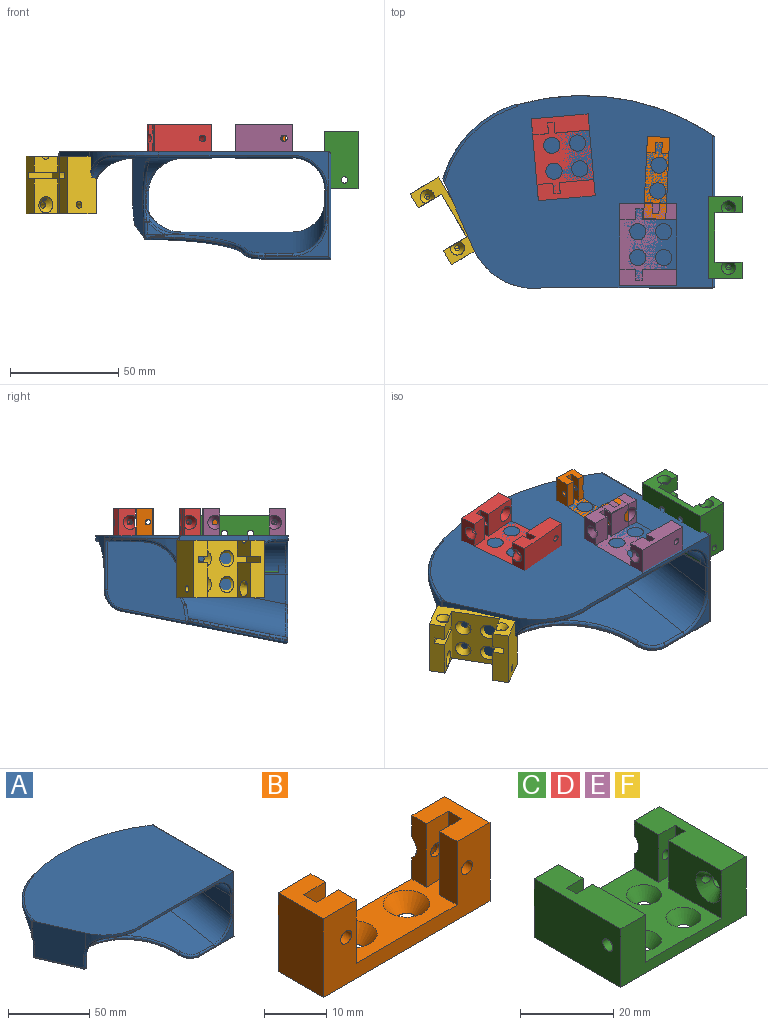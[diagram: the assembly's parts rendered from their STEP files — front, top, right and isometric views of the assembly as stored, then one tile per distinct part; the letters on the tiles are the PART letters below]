
ASSEMBLY  parts=6 mates=3
PART A: 100 faces, bbox 136.9x100.9x51.2 mm
  f0: cylinder r=5mm len=5.41mm, axis (0,-0.19,0.98), area 20.6mm2, adj f1,f2,f13,f83
  f1: bspline ~5.42x5.15mm, area 12.3mm2, adj f0,f2,f13,f60,f78,f84
  f2: plane 10.08x3.37mm, normal (0,0.98,0.19), area 10.7mm2, adj f0,f1,f60,f63
  f3: plane 97.85x87.06mm, normal (0,0,-1), area 6114.5mm2, adj f4,f8,f27,f28,f29,f31,f33,f40
  f4: plane 45.57x36.71mm, normal (-0.99,-0.14,0), area 1163.6mm2, adj f3,f40,f42,f44,f59,f64
  f5: plane 78.53x48.54mm, normal (0,-1,0), area 269.8mm2, adj f12,f19,f34,f38,f39,f46,f47,f48
  f6: cylinder r=107.81mm len=90.77mm, axis (0,0,1), area 314.9mm2, adj f11,f12,f35,f36,f37,f40,f72,f73
  f7: plane 89.44x75.48mm, normal (0,0.19,-0.98), area 2637.8mm2, adj f11,f35,f36,f39,f41,f43,f44,f45
  f8: cylinder r=18.91mm len=29.5mm, axis (0.99,0.14,0), area 177.2mm2, adj f3,f30,f53,f54,f59,f61,f65,f66
  f9: plane 33.93x19.2mm, normal (0.99,0.14,0), area 524.9mm2, adj f14,f15,f33,f53,f61,f70,f71,f72
  f10: plane 59.19x50.35mm, normal (0,-0.19,0.98), area 1600.6mm2, adj f17,f30,f32,f50,f51,f52,f62,f66
  f11: plane 68.7x48.54mm, normal (1,0,0), area 2856.3mm2, adj f6,f7,f35,f37,f38,f39
  f12: plane 123.97x89.25mm, normal (0,0,1), area 9499.2mm2, adj f5,f6,f19,f22,f37,f40,f79
  f13: plane 68.41x19.74mm, normal (-1,0,0), area 730.4mm2, adj f0,f1,f31,f32,f48,f76,f77,f78
  f14: plane 15.18x7.72mm, normal (0,0.98,0.19), area 37.5mm2, adj f9,f15,f60,f61
  f15: plane 28.9x7.23mm, normal (0.99,0.13,0.03), area 44.9mm2, adj f9,f14,f69,f70
  f16: plane 8.4x5.5mm, normal (0,-0.99,0.16), area 20.4mm2, adj f17,f64,f66,f68
  f17: plane 13.1x1.75mm, normal (0,-0.98,-0.19), area 8.4mm2, adj f10,f16,f18,f45,f52,f64
  f18: cylinder r=43.69mm len=43.35mm, axis (0,0.19,-0.98), area 25.3mm2, adj f17,f34,f43,f52
  f19: cylinder r=30.78mm len=32.11mm, axis (0,0,1), area 107.4mm2, adj f5,f12,f22,f85,f86
  f20: plane 2.8x1.15mm, normal (0.99,0.14,0), area 2.6mm2, adj f21,f40,f79,f80
  f21: cylinder r=50.54mm len=34.12mm, axis (0,0,1), area 73.5mm2, adj f20,f79,f80,f81,f82
  f22: plane 31.86x26.8mm, normal (-0.92,-0.4,0), area 902.5mm2, adj f12,f19,f79,f81,f87,f88,f90,f92
  f23: plane 9x0.4mm, normal (-0.2,0.98,0), area 3.7mm2, adj f29,f58,f92,f98
  f24: plane 9x0.37mm, normal (0.4,-0.92,0), area 3.6mm2, adj f27,f55,f56,f88
  f25: plane 29.72x12.99mm, normal (0.92,0.4,0), area 291.9mm2, adj f28,f56,f96,f98
  f26: plane 29.88x13.39mm, normal (0,0,-1), area 13mm2, adj f55,f58,f90,f96
  f27: cylinder r=15mm len=21.22mm, axis (-0.92,-0.4,0), area 128.8mm2, adj f3,f24,f57,f86,f87
  f28: cylinder r=15mm len=62.59mm, axis (0.4,-0.92,0), area 1109.6mm2, adj f3,f25,f57,f99
  f29: cylinder r=15mm len=17.45mm, axis (0.98,0.2,0), area 43.3mm2, adj f3,f23,f82,f93,f99
  f30: bspline ~16.69x14.84mm, area 55mm2, adj f8,f10,f61,f66
  f31: cylinder r=15mm len=77.33mm, axis (0,1,0), area 1716.1mm2, adj f3,f13,f47,f75
  f32: cylinder r=15mm len=52.95mm, axis (0,-0.98,-0.19), area 1164.9mm2, adj f10,f13,f49,f63
  f33: cylinder r=15mm len=55.41mm, axis (0.14,-0.99,0), area 1025.4mm2, adj f3,f9,f54,f73
  f34: bspline ~9.97x8.84mm, area 5.9mm2, adj f5,f18,f41,f51
  f35: bspline ~12.79x11.18mm, area 20.8mm2, adj f6,f7,f11,f77
  f36: bspline ~9.91x8.22mm, area 5.3mm2, adj f6,f7,f42,f70,f71
  f37: cylinder r=1.2mm len=70.71mm, axis (0,-1,0), area 131.4mm2, adj f6,f11,f12,f38
  f38: cylinder r=1.2mm len=49.74mm, axis (0,0,-1), area 91.5mm2, adj f5,f11,f37,f39
  f39: cylinder r=1.2mm len=30.26mm, axis (1,0,0), area 63.2mm2, adj f5,f7,f11,f38,f41
  f40: cylinder r=1.2mm len=25.08mm, axis (0,0,1), area 42.3mm2, adj f3,f4,f6,f12,f20,f42,f79,f80
  f41: bspline ~12.29x9.66mm, area 28.4mm2, adj f7,f34,f39,f43
  f42: bspline ~12.38x10.54mm, area 24mm2, adj f4,f36,f40,f44
  f43: torus R=44.89mm, axis (0,0.19,-0.98), area 120.3mm2, adj f7,f18,f41,f45
  f44: cylinder r=1.2mm len=30.37mm, axis (0.14,-0.97,-0.19), area 58.2mm2, adj f4,f7,f42,f45,f64
  f45: cylinder r=1.2mm len=2.78mm, axis (-1,0,0), area 4.5mm2, adj f7,f17,f43,f44,f64
  f46: cylinder r=1.2mm len=62mm, axis (-1,0,0), area 116.8mm2, adj f3,f5,f47,f85
  f47: torus R=16.2mm, axis (0,-1,0), area 45.7mm2, adj f5,f31,f46,f48
  f48: cylinder r=1.2mm len=13.83mm, axis (0,0,1), area 26.1mm2, adj f5,f13,f47,f49
  f49: bspline ~19.38x16.2mm, area 42.7mm2, adj f5,f32,f48,f50
  f50: cylinder r=1.2mm len=12.47mm, axis (-1,0,0), area 20.6mm2, adj f5,f10,f49,f51
  f51: bspline ~12.28x11.04mm, area 24.3mm2, adj f10,f34,f50,f52
  f52: torus R=44.89mm, axis (0,0.19,-0.98), area 110.5mm2, adj f10,f17,f18,f51
  f53: torus R=20.11mm, axis (-0.99,-0.14,0), area 18.8mm2, adj f8,f9,f54,f61
  f54: bspline ~18.62x18mm, area 21.2mm2, adj f8,f33,f53
  f55: cylinder r=1.2mm len=1.26mm, axis (-0.92,-0.4,0), area 0.8mm2, adj f24,f26,f89,f95
  f56: cylinder r=1.2mm len=9mm, axis (0,0,1), area 17mm2, adj f24,f25,f57,f95
  f57: bspline ~20.85x15.49mm, area 31.4mm2, adj f27,f28,f56
  f58: cylinder r=1.2mm len=1.26mm, axis (0.98,0.2,0), area 0.8mm2, adj f23,f26,f91,f97
  f59: torus R=20.11mm, axis (-0.99,-0.14,0), area 70.2mm2, adj f3,f4,f8,f65
  f60: cylinder r=1.2mm len=83.94mm, axis (1,0,0), area 150.2mm2, adj f1,f2,f7,f14,f62,f69,f84
  f61: bspline ~19.68x13.65mm, area 52.9mm2, adj f8,f9,f14,f30,f53,f62
  f62: cylinder r=1.6mm len=51.53mm, axis (1,0,0), area 129.5mm2, adj f10,f60,f61,f63
  f63: torus R=16.6mm, axis (0,-0.98,-0.19), area 40.2mm2, adj f2,f32,f62,f83
  f64: cylinder r=1.6mm len=8.64mm, axis (0.02,-0.16,-0.99), area 16mm2, adj f4,f16,f17,f44,f45,f65,f67
  f65: bspline ~1.77x1.68mm, area 1.6mm2, adj f8,f59,f64,f67
  f66: bspline ~16.3x8.25mm, area 18.5mm2, adj f8,f10,f16,f30,f68
  f67: bspline ~0.76x0.76mm, area 0.2mm2, adj f64,f65,f68
  f68: bspline ~1.5x0.98mm, area 0.8mm2, adj f8,f16,f66,f67
  f69: cylinder r=1.2mm len=25.05mm, axis (0.14,-0.97,-0.19), area 47.3mm2, adj f7,f15,f60,f70
  f70: bspline ~8.64x4.79mm, area 11.5mm2, adj f9,f15,f36,f69,f71
  f71: bspline ~9.28x4.66mm, area 14.9mm2, adj f9,f36,f70,f72
  f72: cylinder r=1.2mm len=7.26mm, axis (0,0,1), area 14.9mm2, adj f6,f9,f71,f73
  f73: bspline ~18.01x17.92mm, area 47.8mm2, adj f6,f33,f72,f74
  f74: torus R=106.61mm, axis (0,0,-1), area 109.5mm2, adj f3,f6,f73,f75
  f75: bspline ~18.6x17.82mm, area 59.6mm2, adj f6,f31,f74,f76
  f76: cylinder r=1.2mm len=9.83mm, axis (0,0,1), area 25.5mm2, adj f6,f13,f75,f77
  f77: bspline ~12.91x12.9mm, area 35.2mm2, adj f13,f35,f76,f78
  f78: cylinder r=1.2mm len=8.86mm, axis (0,-0.98,-0.19), area 9.6mm2, adj f1,f7,f13,f77,f84
  f79: torus R=49.34mm, axis (0,0,-1), area 95.4mm2, adj f12,f20,f21,f22,f40,f81
  f80: torus R=49.34mm, axis (0,0,-1), area 55.8mm2, adj f3,f20,f21,f40,f82
  f81: cylinder r=1.2mm len=11.69mm, axis (0,0,1), area 9.5mm2, adj f21,f22,f79,f94
  f82: bspline ~21.49x13.34mm, area 36.1mm2, adj f21,f29,f80,f94
  f83: bspline ~13.28x9.18mm, area 35.4mm2, adj f0,f13,f63
  f84: bspline ~4.18x4.05mm, area 4.8mm2, adj f1,f60,f78
  f85: torus R=29.58mm, axis (0,0,-1), area 43.2mm2, adj f3,f19,f46,f86
  f86: bspline ~14.63x13.3mm, area 34.8mm2, adj f19,f27,f85,f87
  f87: torus R=16.2mm, axis (0.92,0.4,0), area 11.3mm2, adj f22,f27,f86,f88
  f88: cylinder r=1.2mm len=9mm, axis (0,0,1), area 17mm2, adj f22,f24,f87,f89
  f89: sphere r=1.2mm, area 2.3mm2, adj f55,f88,f90
  f90: cylinder r=1.2mm len=30.28mm, axis (-0.4,0.92,0), area 61.3mm2, adj f22,f26,f89,f91
  f91: sphere r=1.2mm, area 2.6mm2, adj f58,f90,f92
  f92: cylinder r=1.2mm len=9mm, axis (0,0,1), area 19.2mm2, adj f22,f23,f91,f93
  f93: bspline ~5.67x2.54mm, area 11.7mm2, adj f22,f29,f92,f94
  f94: sphere r=1.2mm, area 0.2mm2, adj f81,f82,f93
  f95: sphere r=1.2mm, area 2mm2, adj f55,f56,f96
  f96: cylinder r=1.2mm len=30.2mm, axis (0.4,-0.92,0), area 61.1mm2, adj f25,f26,f95,f97
  f97: sphere r=1.2mm, area 1.2mm2, adj f58,f96,f98
  f98: cylinder r=1.2mm len=9mm, axis (0,0,1), area 14.7mm2, adj f23,f25,f97,f99
  f99: bspline ~18.02x15.49mm, area 16.4mm2, adj f28,f29,f98
PART B: 28 faces, bbox 38x10.3x15.5 mm
  f0: plane 10.28x7.5mm, normal (0,0,1), area 62.1mm2, adj f5,f7,f10,f12,f13,f14,f26,f27
  f1: plane 10.28x7.5mm, normal (0,0,1), area 62.1mm2, adj f2,f6,f11,f15,f16,f17,f26,f27
  f2: plane 12.5x4mm, normal (-1,0,0), area 50mm2, adj f1,f9,f15,f27
  f3: cylinder r=1.25mm len=4mm, axis (0,1,0), area 31.4mm2, adj f15,f27
  f4: cylinder r=1.25mm len=4mm, axis (0,1,0), area 31.4mm2, adj f14,f27
  f5: plane 15.5x10.28mm, normal (-1,0,0), area 159.4mm2, adj f0,f8,f26,f27
  f6: plane 15.5x10.28mm, normal (1,0,0), area 159.4mm2, adj f1,f8,f26,f27
  f7: plane 12.5x4mm, normal (1,0,0), area 50mm2, adj f0,f9,f14,f27
  f8: plane 38x10.28mm, normal (0,0,-1), area 376.7mm2, adj f5,f6,f22,f24,f26,f27
  f9: plane 33x10.28mm, normal (0,0,1), area 178.2mm2, adj f2,f7,f10,f11,f12,f13,f14,f15
  f10: plane 12.5x3.29mm, normal (1,0,0), area 38.1mm2, adj f0,f9,f12,f21,f26
  f11: plane 12.5x3.29mm, normal (-1,0,0), area 38.1mm2, adj f1,f9,f17,f19,f26
  f12: plane 12.5x5mm, normal (0,-1,0), area 57.6mm2, adj f0,f9,f10,f13,f20
  f13: plane 12.5x3mm, normal (1,0,0), area 37.5mm2, adj f0,f9,f12,f14
  f14: plane 12.5x5mm, normal (0,1,0), area 57.6mm2, adj f0,f4,f7,f9,f13
  f15: plane 12.5x5mm, normal (0,1,0), area 57.6mm2, adj f1,f2,f3,f9,f16
  f16: plane 12.5x3mm, normal (-1,0,0), area 37.5mm2, adj f1,f9,f15,f17
  f17: plane 12.5x5mm, normal (0,-1,0), area 57.6mm2, adj f1,f9,f11,f16,f18
  f18: cylinder r=1.25mm len=2.5mm, axis (0,1,0), area 7mm2, adj f17,f19
  f19: cone r=1.25mm half-angle=37.5deg, axis (0,1,0), area 37.1mm2, adj f11,f18,f26
  f20: cylinder r=1.25mm len=2.5mm, axis (0,1,0), area 7mm2, adj f12,f21
  f21: cone r=1.25mm half-angle=37.5deg, axis (0,1,0), area 37.1mm2, adj f10,f20,f26
  f22: cylinder r=1.5mm len=3mm, axis (0,0,1), area 0.6mm2, adj f8,f23
  f23: cone r=1.5mm half-angle=37.5deg, axis (0,0,1), area 61mm2, adj f9,f22
  f24: cylinder r=1.5mm len=3mm, axis (0,0,1), area 0.6mm2, adj f8,f25
  f25: cone r=1.5mm half-angle=37.5deg, axis (0,0,1), area 61mm2, adj f9,f24
  f26: plane 38x15.5mm, normal (0,1,0), area 246.5mm2, adj f0,f1,f5,f6,f8,f9,f10,f11
  f27: plane 38x15.5mm, normal (0,-1,0), area 291.7mm2, adj f0,f1,f2,f3,f4,f5,f6,f7
PART C: 34 faces, bbox 38x26.4x15.4 mm
  f0: plane 26.4x7.5mm, normal (0,0,1), area 183mm2, adj f2,f4,f11,f13,f15,f16,f17,f33
  f1: plane 26.4x7.5mm, normal (0,0,1), area 183mm2, adj f3,f5,f12,f13,f18,f19,f20,f33
  f2: plane 26.4x15.4mm, normal (-1,0,0), area 399.5mm2, adj f0,f6,f13,f25,f33
  f3: plane 26.4x15.4mm, normal (1,0,0), area 399.5mm2, adj f1,f6,f13,f27,f33
  f4: plane 16x12.5mm, normal (1,0,0), area 155.8mm2, adj f0,f14,f17,f26,f33
  f5: plane 16x12.5mm, normal (-1,0,0), area 155.8mm2, adj f1,f14,f18,f28,f33
  f6: plane 38x26.4mm, normal (0,0,-1), area 974mm2, adj f2,f3,f13,f29,f30,f31,f32,f33
  f7: cylinder r=1.25mm len=9.6mm, axis (0,1,0), area 74.5mm2, adj f8,f18,f28
  f8: cone r=0mm half-angle=59deg, axis (0,1,0), area 3.3mm2, adj f7,f28
  f9: cone r=0mm half-angle=59deg, axis (0,1,0), area 3.3mm2, adj f10,f26
  f10: cylinder r=1.25mm len=9.6mm, axis (0,1,0), area 74.7mm2, adj f9,f17,f26
  f11: plane 12.5x7.4mm, normal (1,0,0), area 88.6mm2, adj f0,f13,f14,f15,f24
  f12: plane 12.5x7.4mm, normal (-1,0,0), area 88.6mm2, adj f1,f13,f14,f20,f22
  f13: plane 38x15.4mm, normal (0,1,0), area 237.8mm2, adj f0,f1,f2,f3,f6,f11,f12,f14
  f14: plane 33x26.4mm, normal (0,0,1), area 460.5mm2, adj f4,f5,f11,f12,f13,f15,f16,f17
  f15: plane 12.5x5mm, normal (0,-1,0), area 57.6mm2, adj f0,f11,f14,f16,f23
  f16: plane 12.5x3mm, normal (1,0,0), area 37.5mm2, adj f0,f14,f15,f17
  f17: plane 12.5x5mm, normal (0,1,0), area 57.6mm2, adj f0,f4,f10,f14,f16
  f18: plane 12.5x5mm, normal (0,1,0), area 57.6mm2, adj f1,f5,f7,f14,f19
  f19: plane 12.5x3mm, normal (-1,0,0), area 37.5mm2, adj f1,f14,f18,f20
  f20: plane 12.5x5mm, normal (0,-1,0), area 57.6mm2, adj f1,f12,f14,f19,f21
  f21: cylinder r=1.25mm len=4.79mm, axis (0,1,0), area 37.6mm2, adj f20,f22
  f22: cone r=1.25mm half-angle=37.5deg, axis (0,1,0), area 41.1mm2, adj f12,f13,f21
  f23: cylinder r=1.25mm len=4.79mm, axis (0,1,0), area 37.6mm2, adj f15,f24
  f24: cone r=1.25mm half-angle=37.5deg, axis (0,1,0), area 41.1mm2, adj f11,f13,f23
  f25: cylinder r=1.5mm len=4.57mm, axis (1,0,0), area 43mm2, adj f2,f26
  f26: cone r=1.5mm half-angle=37.5deg, axis (1,0,0), area 58.5mm2, adj f4,f9,f10,f25
  f27: cylinder r=1.5mm len=4.57mm, axis (-1,0,0), area 43mm2, adj f3,f28
  f28: cone r=1.5mm half-angle=37.5deg, axis (-1,0,0), area 58.3mm2, adj f5,f7,f8,f27
  f29: cone r=1.5mm half-angle=37.5deg, axis (0,0,1), area 60.6mm2, adj f6,f14
  f30: cone r=1.5mm half-angle=37.5deg, axis (0,0,1), area 60.6mm2, adj f6,f14
  f31: cone r=1.5mm half-angle=37.5deg, axis (0,0,1), area 60.6mm2, adj f6,f14
  f32: cone r=1.5mm half-angle=37.5deg, axis (0,0,1), area 60.6mm2, adj f6,f14
  f33: plane 38x15.4mm, normal (0,-1,0), area 297.7mm2, adj f0,f1,f2,f3,f4,f5,f6,f14
PART D: same geometry as C
PART E: same geometry as C
PART F: same geometry as C
PLACE A t=(-46.4,85,-16)mm
PLACE B rot(axis=(0,0,-1),92.8deg) t=(-32.17,51.11,12.5)mm
PLACE C rot(axis=(0.58,0.58,0.58),120deg) t=(12.5,23.25,-5.02)mm
PLACE D rot(axis=(0,0,1),95deg) t=(-69.03,60.51,12.5)mm
PLACE E rot(axis=(0,0,1),90deg) t=(-29.71,20.03,12.5)mm
PLACE F rot(axis=(0.78,-0.45,-0.45),104.3deg) t=(-131.52,27.14,-16.57)mm
MATE planar B.f9 <-> A.f12  axis (0,0,1) through (-27.4,50.88,0)mm
MATE planar E.f14 <-> A.f12  axis (0,0,1) through (-31.65,20.03,0)mm
MATE planar C.f14 <-> A.f11  axis (1,0,0) through (0,23.25,-3.08)mm
